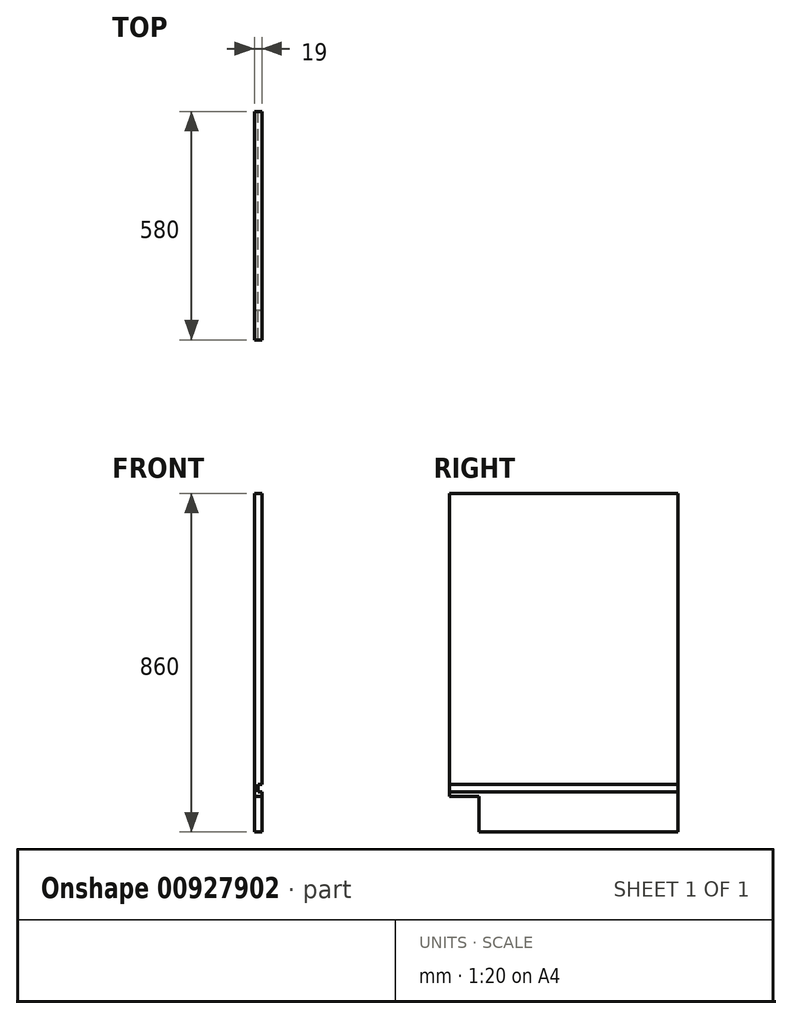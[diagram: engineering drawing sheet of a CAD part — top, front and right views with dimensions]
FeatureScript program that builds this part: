
annotation { "Feature Type Name" : "Feature", "Feature Type Description" : "" }
export const myFeature = defineFeature(function(context is Context, id is Id, definition is map)
    precondition{}
    {
        {
            var Q0;
            Q0=qCreatedBy(makeId("Right.planeOp"),FACE);
            var sketch = newSketch(context, id + "F0", { "sketchPlane" : qUnion([Q0])});
            skLineSegment(sketch, "E0.bottom", {"start": v(0, 0) * mm, "end": v(-505, 0) * mm});
            skLineSegment(sketch, "E0.top", {"start": v(0, 860) * mm, "end": v(-580, 860) * mm});
            skLineSegment(sketch, "E0.left", {"start": v(0, 0) * mm, "end": v(0, 860) * mm});
            skLineSegment(sketch, "E0.right", {"start": v(-580, 90) * mm, "end": v(-580, 860) * mm});
            skLineSegment(sketch, "E1", {"start": v(-580, 90) * mm, "end": v(-505, 90) * mm});
            skLineSegment(sketch, "E2", {"start": v(-505, 90) * mm, "end": v(-505, 0) * mm});
            skSolve(sketch);
        }
        {
            var Q0;
            Q0 = qSketchRegion(id + "F0", true);
            extrude(context, id + "F1", {"entities" : qUnion([Q0]), "depth" : 19 * mm, "offsetDistance" : 25 * mm});
        }
        {
            var Q0;
            Q0=qCreatedBy(makeId("Front.planeOp"),FACE);
            var sketch = newSketch(context, id + "F2", { "sketchPlane" : qUnion([Q0])});
            skLineSegment(sketch, "E3.0", {"start": v(19, 90) * mm, "end": v(19, 860) * mm, "construction": true});
            skLineSegment(sketch, "E4.0", {"start": v(19, 90) * mm, "end": v(0, 90) * mm, "construction": true});
            skPoint(sketch, "E5.oppositeSnap0", {"position": v(9.5, 90) * mm});
            skLineSegment(sketch, "E5.bottom", {"start": v(19, 102) * mm, "end": v(9.5, 102) * mm});
            skLineSegment(sketch, "E5.top", {"start": v(19, 121) * mm, "end": v(9.5, 121) * mm});
            skLineSegment(sketch, "E5.left", {"start": v(19, 102) * mm, "end": v(19, 121) * mm});
            skLineSegment(sketch, "E5.right", {"start": v(9.5, 102) * mm, "end": v(9.5, 121) * mm});
            skSolve(sketch);
        }
        {
            var Q0;
            Q0 = qSketchRegion(id + "F2", true);
            extrude(context, id + "F3", {"entities" : qUnion([Q0]), "operationType" : NewBodyOperationType.REMOVE, "endBound" : BoundingType.THROUGH_ALL, "depth" : 25 * mm, "offsetDistance" : 25 * mm});
        }
    });
